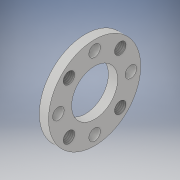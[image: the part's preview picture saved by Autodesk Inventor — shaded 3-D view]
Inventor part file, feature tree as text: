
AUTODESK INVENTOR PART (.ipt)
format: ipt  version: 2019 (Build 230136000, 136)  size: 137,728 bytes
history: native  units: in
note: dims shown in document units (in); Inventor stores cm internally (conversion verified against a paired STEP export)
features: extrude x3, sketch x3, pattern_circular x2, thread x1
ambient origin geometry x8: Origin, YZ Plane, XZ Plane, XY Plane, X Axis, Y Axis, Z Axis, Center Point
bodies: Solid1 (feature_tree)
feature tree (9):
  extrude  "Extrusion1"  Depth=0.1575in TaperAngle=0.0deg
  extrude  "Extrusion2"  Depth=0.6201in
  pattern_circular  "Circular Pattern1"  [2 undecoded]
  extrude  "Extrusion3"  Depth=0.3937in TaperAngle=360.0deg
  thread  "Thread1"  [1 undecoded]
  pattern_circular  "Circular Pattern2"  Angle=45.0deg  [1 undecoded]
  sketch  "Sketch1"  dims[d0=0.7874in d1=0.1575in d2=0.0in]
  sketch  "Sketch3"  dims[d3=1.5748in d4=0.6201in]
  sketch  "Sketch4"  dims[d5=0.1969in d6=0.1575in d7=0.0in d8=1.5748in d9=360.0deg d11=0.6201in d12=45.0deg d13=0.1969in d14=0.1575in d15=0.0in d16=0.3937in d17=0.0in d18=1.5748in d19=360.0deg]
note: 4 required parameter values undecoded (feature->parameter linkage not recoverable at this tier; creation-order binding heuristic only, values carry confidence <= 0.55)
